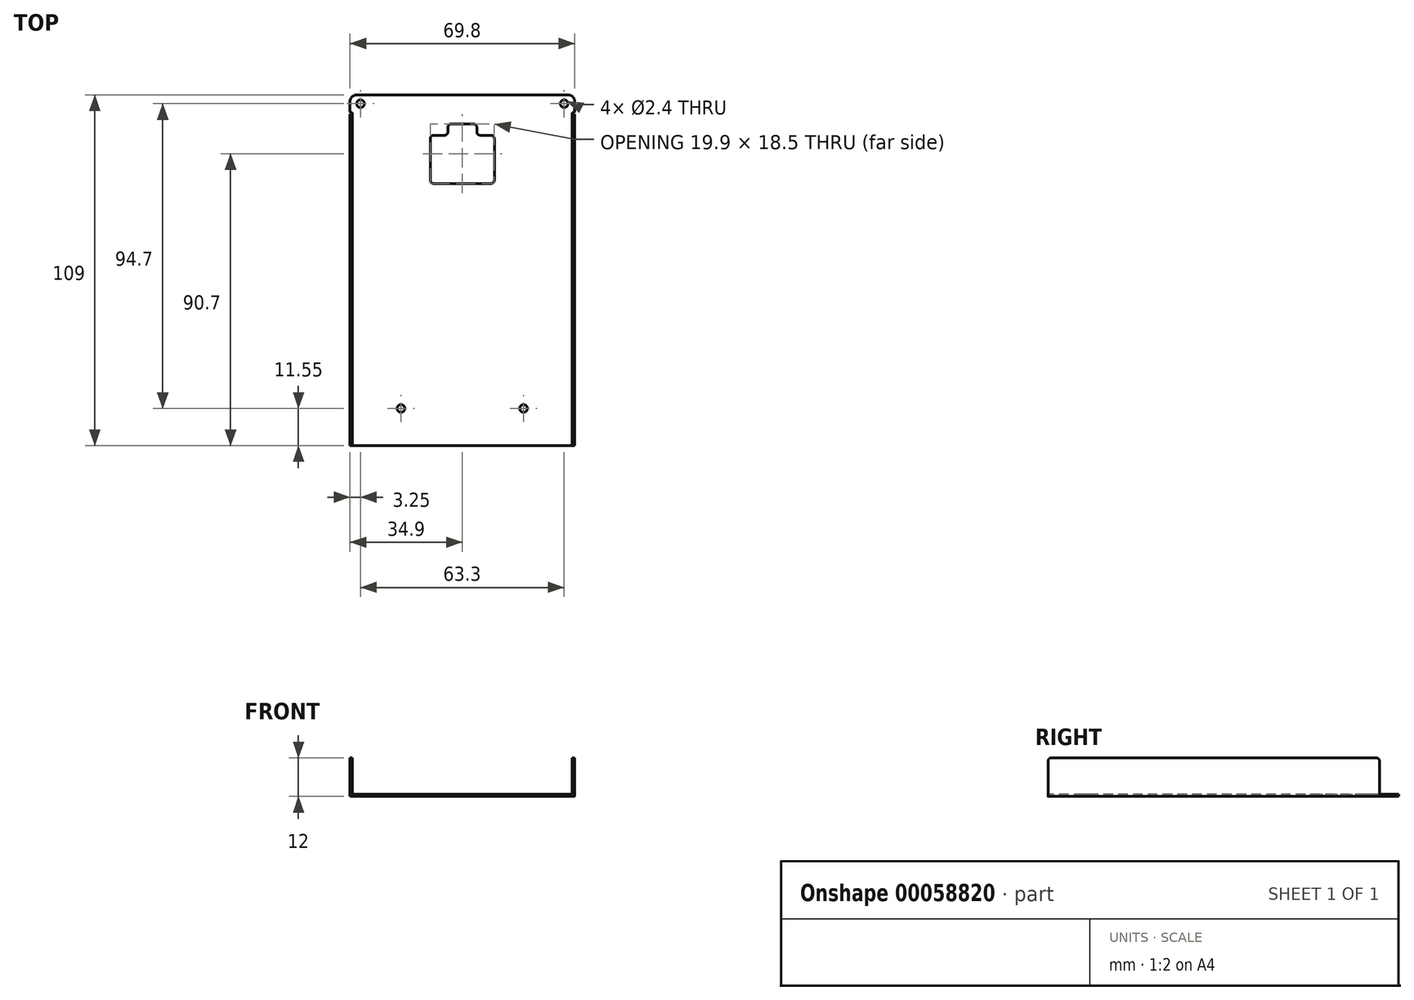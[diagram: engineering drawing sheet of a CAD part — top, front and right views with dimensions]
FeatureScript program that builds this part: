
annotation { "Feature Type Name" : "Feature", "Feature Type Description" : "" }
export const myFeature = defineFeature(function(context is Context, id is Id, definition is map)
    precondition{}
    {
        {
            assignVariable(context, id + "F0", {"name" : "MaterialThickness", "anyValue" : 0.74 * mm});
        }
        {
            var Q0;
            Q0=qCreatedBy(makeId("Top.planeOp"),FACE);
            var sketch = newSketch(context, id + "F1", { "sketchPlane" : qUnion([Q0])});
            skLineSegment(sketch, "E0", {"start": v(30.3, -54.5) * mm, "end": v(30.3, 52.5) * mm});
            skLineSegment(sketch, "E1", {"start": v(-39.5, -54.5) * mm, "end": v(-39.5, 52.5) * mm});
            skLineSegment(sketch, "E2", {"start": v(-37.5, 54.5) * mm, "end": v(28.3, 54.5) * mm});
            skLineSegment(sketch, "E3", {"start": v(-39.5, -54.5) * mm, "end": v(30.3, -54.5) * mm});
            skCircle(sketch, "E4", {"center": v(-36.25, 51.75) * mm, "radius": 1.2 * mm});
            skCircle(sketch, "E5", {"center": v(27.05, 51.75) * mm, "radius": 1.2 * mm});
            skCircle(sketch, "E6", {"center": v(14.45, -42.95) * mm, "radius": 1.2 * mm});
            skCircle(sketch, "E7", {"center": v(-23.65, -42.95) * mm, "radius": 1.2 * mm});
            skPoint(sketch, "E8.visualSharp", {"position": v(-39.5, 54.5) * mm});
            skArc(sketch, "E8.filletArc", {"start": v(-37.5, 54.5) * mm, "mid": v(-38.91, 53.91) * mm, "end": v(-39.5, 52.5) * mm});
            skPoint(sketch, "E9.visualSharp", {"position": v(30.3, 54.5) * mm});
            skArc(sketch, "E9.filletArc", {"start": v(30.3, 52.5) * mm, "mid": v(29.71, 53.91) * mm, "end": v(28.3, 54.5) * mm});
            skLineSegment(sketch, "E10.rect.bottom", {"start": v(3.75, 31.45) * mm, "end": v(-12.95, 31.45) * mm, "construction": true});
            skLineSegment(sketch, "E10.rect.top", {"start": v(3.75, 37.95) * mm, "end": v(-12.95, 37.95) * mm, "construction": true});
            skLineSegment(sketch, "E10.rect.left", {"start": v(3.75, 31.45) * mm, "end": v(3.75, 37.95) * mm, "construction": true});
            skLineSegment(sketch, "E10.rect.right", {"start": v(-12.95, 31.45) * mm, "end": v(-12.95, 37.95) * mm, "construction": true});
            skPoint(sketch, "E10.rect.middle", {"position": v(-4.6, 34.7) * mm});
            skPoint(sketch, "E11.visualSharp", {"position": v(-12.95, 37.95) * mm});
            skPoint(sketch, "E12.visualSharp", {"position": v(-12.95, 31.45) * mm});
            skPoint(sketch, "E13.visualSharp", {"position": v(3.75, 31.45) * mm});
            skPoint(sketch, "E14.visualSharp", {"position": v(3.75, 37.95) * mm});
            skLineSegment(sketch, "E15", {"start": v(-4.6, 54.5) * mm, "end": v(-4.6, 0) * mm, "construction": true});
            skPoint(sketch, "E15.endSnap0", {"position": v(-4.6, 29.15) * mm});
            skLineSegment(sketch, "E16.0", {"start": v(4.35, 41.95) * mm, "end": v(0.9, 41.95) * mm});
            skLineSegment(sketch, "E16.1", {"start": v(5.35, 27.95) * mm, "end": v(5.35, 40.95) * mm});
            skLineSegment(sketch, "E16.2", {"start": v(4.35, 26.95) * mm, "end": v(-13.55, 26.95) * mm});
            skLineSegment(sketch, "E16.3", {"start": v(-14.55, 27.95) * mm, "end": v(-14.55, 40.95) * mm});
            skLineSegment(sketch, "E17", {"start": v(-4.6, 45.45) * mm, "end": v(-8.1, 45.45) * mm});
            skLineSegment(sketch, "E18", {"start": v(-9.1, 44.45) * mm, "end": v(-9.1, 42.95) * mm});
            skLineSegment(sketch, "E19.MirrorCS", {"start": v(-4.6, 45.45) * mm, "end": v(-1.1, 45.45) * mm});
            skLineSegment(sketch, "E20.MirrorCS", {"start": v(-0.1, 44.45) * mm, "end": v(-0.1, 42.95) * mm});
            skLineSegment(sketch, "E21.trimOffspring", {"start": v(-10.1, 41.95) * mm, "end": v(-13.55, 41.95) * mm});
            skPoint(sketch, "E22.visualSharp", {"position": v(-9.1, 45.45) * mm});
            skArc(sketch, "E22.filletArc", {"start": v(-8.1, 45.45) * mm, "mid": v(-8.8, 45.16) * mm, "end": v(-9.1, 44.45) * mm});
            skPoint(sketch, "E23.visualSharp", {"position": v(-0.1, 45.45) * mm});
            skArc(sketch, "E23.filletArc", {"start": v(-0.1, 44.45) * mm, "mid": v(-0.4, 45.16) * mm, "end": v(-1.1, 45.45) * mm});
            skPoint(sketch, "E24.visualSharp", {"position": v(5.35, 41.95) * mm});
            skArc(sketch, "E24.filletArc", {"start": v(5.35, 40.95) * mm, "mid": v(5.06, 41.66) * mm, "end": v(4.35, 41.95) * mm});
            skPoint(sketch, "E25.visualSharp", {"position": v(-14.55, 41.95) * mm});
            skArc(sketch, "E25.filletArc", {"start": v(-13.55, 41.95) * mm, "mid": v(-14.26, 41.66) * mm, "end": v(-14.55, 40.95) * mm});
            skPoint(sketch, "E26.visualSharp", {"position": v(-14.55, 26.95) * mm});
            skArc(sketch, "E26.filletArc", {"start": v(-14.55, 27.95) * mm, "mid": v(-14.26, 27.24) * mm, "end": v(-13.55, 26.95) * mm});
            skPoint(sketch, "E27.visualSharp", {"position": v(5.35, 26.95) * mm});
            skArc(sketch, "E27.filletArc", {"start": v(4.35, 26.95) * mm, "mid": v(5.06, 27.24) * mm, "end": v(5.35, 27.95) * mm});
            skPoint(sketch, "E28.visualSharp", {"position": v(-9.1, 41.95) * mm});
            skArc(sketch, "E28.filletArc", {"start": v(-10.1, 41.95) * mm, "mid": v(-9.4, 42.24) * mm, "end": v(-9.1, 42.95) * mm});
            skPoint(sketch, "E29.visualSharp", {"position": v(-0.1, 41.95) * mm});
            skArc(sketch, "E29.filletArc", {"start": v(-0.1, 42.95) * mm, "mid": v(0.2, 42.24) * mm, "end": v(0.9, 41.95) * mm});
            skSolve(sketch);
        }
        {
            var Q0;
            Q0=qSketchRegion(id+"F1",true);
            extrude(context, id + "F2", {"entities" : qUnion([Q0]), "depth" : getVariable(context, 'MaterialThickness')});
        }
        {
            var Q0;
            Q0=makeQuery(id+"F2.opExtrude","CAP_FACE",FACE,{"disambiguationData":[OSD([sQuery(id+"F1.wireOp",EDGE,"E0"),sQuery(id+"F1.wireOp",EDGE,"E1"),sQuery(id+"F1.wireOp",EDGE,"E2"),sQuery(id+"F1.wireOp",EDGE,"6f542626-f2fe-4e62-9dc8-af51138589b2"),sQuery(id+"F1.wireOp",EDGE,"d65317cd-7c6a-42e4-b09b-290c2fcee52c"),sQuery(id+"F1.wireOp",EDGE,"40293471-6695-460b-ad5e-70b06ef1c56a"),sQuery(id+"F1.wireOp",EDGE,"0b21d12f-ddd4-4e10-89e9-105603cf3b6e"),sQuery(id+"F1.wireOp",EDGE,"79ee2fa8-379d-4bab-a302-94835cc6177e"),sQuery(id+"F1.wireOp",EDGE,"5b2d6fb2-da7a-4bf0-967d-20eb2f197081"),sQuery(id+"F1.wireOp",EDGE,"58eab4bf-ed62-4cde-a4af-ce179843e936"),sQuery(id+"F1.wireOp",EDGE,"bd959c86-ba9c-48ce-8a67-1202fe78da0e"),sQuery(id+"F1.wireOp",EDGE,"4cee920a-c67d-4b1d-aa53-96ac32e3495d"),sQuery(id+"F1.wireOp",EDGE,"0f1fe42c-9a65-4718-9d6c-7e304eec8dc9"),sQuery(id+"F1.wireOp",EDGE,"41df9827-cfb7-4644-8396-7d36da1e9611"),sQuery(id+"F1.wireOp",EDGE,"012ba0f6-2408-4579-9935-ac00b418ca78"),sQuery(id+"F1.wireOp",EDGE,"a6d1a8ff-5993-4480-aa68-b251ac2e3773"),sQuery(id+"F1.wireOp",EDGE,"90826518-7ab9-4a11-9cb2-50551e0b17c5"),sQuery(id+"F1.wireOp",EDGE,"dec4adf2-c5f8-4cf7-9b65-f65938c339f3"),sQuery(id+"F1.wireOp",EDGE,"6aff881b-a8da-4633-8748-1f352a3986aa"),sQuery(id+"F1.wireOp",EDGE,"6b8bf9ce-d740-4018-889f-3fed14afc211"),sQuery(id+"F1.wireOp",EDGE,"4c5e473f-9d43-4600-b7a0-6199b0060a3d"),sQuery(id+"F1.wireOp",EDGE,"50cb06d5-be9d-4216-865b-45e0080ed08e"),sQuery(id+"F1.wireOp",EDGE,"7cdb9ee0-e2e8-45ac-8bdb-5b1d0834dcd6"),sQuery(id+"F1.wireOp",EDGE,"752c73df-f6f7-48e6-814b-9abc70d4c3b5"),sQuery(id+"F1.wireOp",EDGE,"d4403edb-6ecc-4fb8-9abe-a5cf43e54ecf"),sQuery(id+"F1.wireOp",EDGE,"191c357e-7506-4e18-90b4-bb71a73d584a"),sQuery(id+"F1.wireOp",EDGE,"36182ddf-d56b-4a3d-8339-a1267bb4d182"),sQuery(id+"F1.wireOp",EDGE,"3cfc1f5f-f39c-4474-8388-3dd97f5584c0"),sQuery(id+"F1.wireOp",EDGE,"4c48c394-4fa5-4c5e-9177-710229550736"),sQuery(id+"F1.wireOp",EDGE,"7cbb6381-f1a6-487e-88ab-7a4eef711d66"),sQuery(id+"F1.wireOp",EDGE,"5dec03ee-e572-469c-8b05-a0337d8c623c"),sQuery(id+"F1.wireOp",EDGE,"d16cefb8-363f-4407-b9f5-a53e7ae9c1b3"),sQuery(id+"F1.wireOp",EDGE,"E3"),sQuery(id+"F1.wireOp",EDGE,"E4"),sQuery(id+"F1.wireOp",EDGE,"E5"),sQuery(id+"F1.wireOp",EDGE,"E6"),sQuery(id+"F1.wireOp",EDGE,"E7"),sQuery(id+"F1.wireOp",EDGE,"49b4b471-93f8-46f3-9035-a445390ed24f"),sQuery(id+"F1.wireOp",EDGE,"013d988c-518a-43cd-931a-afb82e042039"),sQuery(id+"F1.wireOp",EDGE,"b009fba4-9d74-487f-b1b2-e77be794c7df"),sQuery(id+"F1.wireOp",EDGE,"f28ca319-59c4-4176-9a6a-b8e9c12ca7b2"),sQuery(id+"F1.wireOp",EDGE,"59ab4c71-fb57-451b-a7bc-e024e530d7a6"),sQuery(id+"F1.wireOp",EDGE,"47252107-bac6-4eb8-93b8-c023fa44c8e8"),sQuery(id+"F1.wireOp",EDGE,"b80df239-3f1f-4e86-9030-635545e30786"),sQuery(id+"F1.wireOp",EDGE,"baca6f1a-d7fb-4206-b7a5-cbdfadded3ed"),sQuery(id+"F1.wireOp",EDGE,"d976eecf-eaf4-4cce-8532-cadcb9868e27"),sQuery(id+"F1.wireOp",EDGE,"4569245a-5ea1-4106-908f-afcd5ec1f1bc"),sQuery(id+"F1.wireOp",EDGE,"a88b5052-fa65-4c67-8c1e-17682c5e5b6b"),sQuery(id+"F1.wireOp",EDGE,"c3202e9f-e72c-49b5-b375-3782fcdd84b2"),sQuery(id+"F1.wireOp",EDGE,"ae9a4485-fe66-418c-99cf-f2badf27484e"),sQuery(id+"F1.wireOp",EDGE,"40ff1a60-ad1b-470d-9941-3648aebe8ce7"),sQuery(id+"F1.wireOp",EDGE,"7efc5e7b-d0f8-4c2e-be74-3157bb2b81f2"),sQuery(id+"F1.wireOp",EDGE,"a604e65e-d63e-4fcf-87a2-1d68459ffd2f"),sQuery(id+"F1.wireOp",EDGE,"9b040391-65f2-4517-89ec-09136afad379"),sQuery(id+"F1.wireOp",EDGE,"e81865d5-4931-4b27-a9b8-568d70e091ed"),sQuery(id+"F1.wireOp",EDGE,"33fbec23-d60a-44ca-a5ed-6a9adadaf32d"),sQuery(id+"F1.wireOp",EDGE,"d18368f3-3517-4bad-a039-cce0df7d30f8"),sQuery(id+"F1.wireOp",EDGE,"adf0adf2-995a-4c73-9a9f-0c34d5a06e90"),sQuery(id+"F1.wireOp",EDGE,"8d4f8d75-ff03-45a9-8da5-e2bfa5d89cf8"),sQuery(id+"F1.wireOp",EDGE,"0def6ea3-42c0-499a-87a9-d967d37a2398"),sQuery(id+"F1.wireOp",EDGE,"418a7f11-9ba6-4330-9219-449a15997eb1"),sQuery(id+"F1.wireOp",EDGE,"19beec09-856a-4503-8090-15e2c865af76"),sQuery(id+"F1.wireOp",EDGE,"f8c1126e-abe4-42b3-b083-fbb39cc2f8dd"),sQuery(id+"F1.wireOp",EDGE,"511b526c-3d0c-4ee1-8060-97b439644142"),sQuery(id+"F1.wireOp",EDGE,"77a7ece0-8d82-497c-bc19-0a22f7db5636"),sQuery(id+"F1.wireOp",EDGE,"9b200ce0-63a7-49f5-a05a-f950ba5009f6"),sQuery(id+"F1.wireOp",EDGE,"11c32315-20c8-4d77-a798-f002eaef5331"),sQuery(id+"F1.wireOp",EDGE,"23f4386d-157d-49f5-b0b6-e080ac96bcf1"),sQuery(id+"F1.wireOp",EDGE,"c1e70f36-b0bc-4dd7-b00e-9526c5c15aa3"),sQuery(id+"F1.wireOp",EDGE,"f1081c25-ebe6-49c4-9bd5-8d7a2e5cd1f3"),sQuery(id+"F1.wireOp",EDGE,"baca9122-060d-4abe-9427-23689144884f"),sQuery(id+"F1.wireOp",EDGE,"E8.filletArc"),sQuery(id+"F1.wireOp",EDGE,"E9.filletArc")])],"isStart":true});
            var sketch = newSketch(context, id + "F3", { "sketchPlane" : qUnion([Q0])});
            skLineSegment(sketch, "E30.bottom", {"start": v(30.3, 54.5) * mm, "end": v(29.56, 54.5) * mm});
            skLineSegment(sketch, "E30.top", {"start": v(30.3, -48.5) * mm, "end": v(29.56, -48.5) * mm});
            skLineSegment(sketch, "E30.left", {"start": v(30.3, 54.5) * mm, "end": v(30.3, -48.5) * mm});
            skLineSegment(sketch, "E30.right", {"start": v(29.56, 54.5) * mm, "end": v(29.56, -48.5) * mm});
            skLineSegment(sketch, "E31.bottom", {"start": v(-39.5, 54.5) * mm, "end": v(-38.76, 54.5) * mm});
            skLineSegment(sketch, "E31.top", {"start": v(-39.5, -48.5) * mm, "end": v(-38.76, -48.5) * mm});
            skLineSegment(sketch, "E31.left", {"start": v(-39.5, 54.5) * mm, "end": v(-39.5, -48.5) * mm});
            skLineSegment(sketch, "E31.right", {"start": v(-38.76, 54.5) * mm, "end": v(-38.76, -48.5) * mm});
            skSolve(sketch);
        }
        {
            var Q0;
            Q0=qSketchRegion(id+"F3",true);
            extrude(context, id + "F4", {"entities" : qUnion([Q0]), "operationType" : NewBodyOperationType.ADD, "oppositeDirection" : true, "depth" : 12 * mm});
        }
        {
            var Q0;
            Q0=makeQuery(id+"F4.opExtrude","CAP_EDGE",EDGE,{"disambiguationData":[OSD([sQuery(id+"F3.wireOp",EDGE,"E30.bottom")])],"isStart":false});
            var Q1;
            Q1=makeQuery(id+"F4.opExtrude","CAP_EDGE",EDGE,{"disambiguationData":[OSD([sQuery(id+"F3.wireOp",EDGE,"E30.top")])],"isStart":false});
            var Q2;
            Q2=makeQuery(id+"F4.opExtrude","CAP_EDGE",EDGE,{"disambiguationData":[OSD([sQuery(id+"F3.wireOp",EDGE,"E31.top")])],"isStart":false});
            var Q3;
            Q3=makeQuery(id+"F4.opExtrude","CAP_EDGE",EDGE,{"disambiguationData":[OSD([sQuery(id+"F3.wireOp",EDGE,"E31.bottom")])],"isStart":false});
            fillet(context, id + "F5", {"entities" : qUnion([Q0, Q1, Q2, Q3]), "radius" : 1 * mm, "tangentPropagation" : true, "allowEdgeOverflow" : false});
        }
        {
            var Q0;
            Q0=makeQuery(id+"F2.opExtrude","CAP_FACE",FACE,{"disambiguationData":[OSD([sQuery(id+"F1.wireOp",EDGE,"E0"),sQuery(id+"F1.wireOp",EDGE,"E1"),sQuery(id+"F1.wireOp",EDGE,"E2"),sQuery(id+"F1.wireOp",EDGE,"E3"),sQuery(id+"F1.wireOp",EDGE,"E4"),sQuery(id+"F1.wireOp",EDGE,"E5"),sQuery(id+"F1.wireOp",EDGE,"E6"),sQuery(id+"F1.wireOp",EDGE,"E7"),sQuery(id+"F1.wireOp",EDGE,"E8.filletArc"),sQuery(id+"F1.wireOp",EDGE,"E9.filletArc"),sQuery(id+"F1.wireOp",EDGE,"15ddee82-5b16-4217-afd7-89f68c77764c.0"),sQuery(id+"F1.wireOp",EDGE,"15ddee82-5b16-4217-afd7-89f68c77764c.1"),sQuery(id+"F1.wireOp",EDGE,"15ddee82-5b16-4217-afd7-89f68c77764c.2"),sQuery(id+"F1.wireOp",EDGE,"15ddee82-5b16-4217-afd7-89f68c77764c.3"),sQuery(id+"F1.wireOp",EDGE,"15ddee82-5b16-4217-afd7-89f68c77764c.4"),sQuery(id+"F1.wireOp",EDGE,"15ddee82-5b16-4217-afd7-89f68c77764c.5"),sQuery(id+"F1.wireOp",EDGE,"15ddee82-5b16-4217-afd7-89f68c77764c.6"),sQuery(id+"F1.wireOp",EDGE,"15ddee82-5b16-4217-afd7-89f68c77764c.7")])],"isStart":false});
            var sketch = newSketch(context, id + "F6", { "sketchPlane" : qUnion([Q0])});
            skLineSegment(sketch, "E32.bottom", {"start": v(-39.5, 48.5) * mm, "end": v(-38.76, 48.5) * mm});
            skLineSegment(sketch, "E32.top", {"start": v(-39.5, 49) * mm, "end": v(-38.76, 49) * mm});
            skLineSegment(sketch, "E32.left", {"start": v(-39.5, 48.5) * mm, "end": v(-39.5, 49) * mm});
            skLineSegment(sketch, "E32.right", {"start": v(-38.76, 48.5) * mm, "end": v(-38.76, 49) * mm});
            skLineSegment(sketch, "E33.bottom", {"start": v(30.3, 48.5) * mm, "end": v(29.56, 48.5) * mm});
            skLineSegment(sketch, "E33.top", {"start": v(30.3, 49) * mm, "end": v(29.56, 49) * mm});
            skLineSegment(sketch, "E33.left", {"start": v(30.3, 48.5) * mm, "end": v(30.3, 49) * mm});
            skLineSegment(sketch, "E33.right", {"start": v(29.56, 48.5) * mm, "end": v(29.56, 49) * mm});
            skSolve(sketch);
        }
        {
            var Q0;
            Q0=qSketchRegion(id+"F6",true);
            extrude(context, id + "F7", {"entities" : qUnion([Q0]), "operationType" : NewBodyOperationType.REMOVE, "oppositeDirection" : true, "depth" : 25 * mm});
        }
        {
            var Q0;
            Q0=makeQuery(id+"F7.boolean.opBoolean","COPY",EDGE,{"derivedFrom":makeQuery(id+"F7.opExtrude","SWEPT_EDGE",EDGE,{"disambiguationData":[OSD([sQuery(id+"F1.wireOp",EDGE,"E0"),sQuery(id+"F6.wireOp",EDGE,"E33.top"),sQuery(id+"F6.wireOp",EDGE,"E33.left")])]})});
            var Q1;
            Q1=makeQuery(id+"F7.boolean.opBoolean","COPY",EDGE,{"derivedFrom":makeQuery(id+"F7.opExtrude","SWEPT_EDGE",EDGE,{"disambiguationData":[OSD([sQuery(id+"F6.wireOp",EDGE,"E33.top"),sQuery(id+"F6.wireOp",EDGE,"E33.right")])]})});
            var Q2;
            Q2=makeQuery(id+"F7.boolean.opBoolean","COPY",EDGE,{"derivedFrom":makeQuery(id+"F7.opExtrude","SWEPT_EDGE",EDGE,{"disambiguationData":[OSD([sQuery(id+"F1.wireOp",EDGE,"E1"),sQuery(id+"F6.wireOp",EDGE,"E32.top"),sQuery(id+"F6.wireOp",EDGE,"E32.left")])]})});
            var Q3;
            Q3=makeQuery(id+"F7.boolean.opBoolean","COPY",EDGE,{"derivedFrom":makeQuery(id+"F7.opExtrude","SWEPT_EDGE",EDGE,{"disambiguationData":[OSD([sQuery(id+"F6.wireOp",EDGE,"E32.top"),sQuery(id+"F6.wireOp",EDGE,"E32.right")])]})});
            fillet(context, id + "F8", {"entities" : qUnion([Q0, Q1, Q2, Q3]), "radius" : .3 * mm, "tangentPropagation" : true, "allowEdgeOverflow" : false});
        }
        {
            var Q0;
            {var subQ0=sQuery(id+"F1.wireOp",EDGE,"E3");var subQ1=sQuery(id+"F1.wireOp",EDGE,"E1");Q0=makeQuery(id+"F7.boolean.opBoolean","SPLIT",EDGE,{"disambiguationData":[TD([makeQuery(id+"F2.opExtrude","SWEPT_FACE",FACE,{"disambiguationData":[OSD([subQ0])]})])],"derivedFrom":makeQuery(id+"F2.opExtrude","CAP_EDGE",EDGE,{"disambiguationData":[OSD([subQ1])],"isStart":true})});}
            var Q1;
            {var subQ0=sQuery(id+"F1.wireOp",EDGE,"E3");var subQ1=sQuery(id+"F1.wireOp",EDGE,"E0");Q1=makeQuery(id+"F7.boolean.opBoolean","SPLIT",EDGE,{"disambiguationData":[TD([makeQuery(id+"F2.opExtrude","SWEPT_FACE",FACE,{"disambiguationData":[OSD([subQ0])]})])],"derivedFrom":makeQuery(id+"F2.opExtrude","CAP_EDGE",EDGE,{"disambiguationData":[OSD([subQ1])],"isStart":true})});}
            fillet(context, id + "F9", {"entities" : qUnion([Q0, Q1]), "radius" : .65 * mm, "tangentPropagation" : true, "allowEdgeOverflow" : false});
        }
        {
            var Q0;
            Q0=makeQuery(id+"F4.boolean.opBoolean","INTERSECT",EDGE,{"derivedFrom":[makeQuery(id+"F2.opExtrude","CAP_FACE",FACE,{"disambiguationData":[OSD([sQuery(id+"F1.wireOp",EDGE,"E0"),sQuery(id+"F1.wireOp",EDGE,"E1"),sQuery(id+"F1.wireOp",EDGE,"E2"),sQuery(id+"F1.wireOp",EDGE,"E3"),sQuery(id+"F1.wireOp",EDGE,"E4"),sQuery(id+"F1.wireOp",EDGE,"E5"),sQuery(id+"F1.wireOp",EDGE,"E6"),sQuery(id+"F1.wireOp",EDGE,"E7"),sQuery(id+"F1.wireOp",EDGE,"E8.filletArc"),sQuery(id+"F1.wireOp",EDGE,"E9.filletArc"),sQuery(id+"F1.wireOp",EDGE,"15ddee82-5b16-4217-afd7-89f68c77764c.0"),sQuery(id+"F1.wireOp",EDGE,"15ddee82-5b16-4217-afd7-89f68c77764c.1"),sQuery(id+"F1.wireOp",EDGE,"15ddee82-5b16-4217-afd7-89f68c77764c.2"),sQuery(id+"F1.wireOp",EDGE,"15ddee82-5b16-4217-afd7-89f68c77764c.3"),sQuery(id+"F1.wireOp",EDGE,"15ddee82-5b16-4217-afd7-89f68c77764c.4"),sQuery(id+"F1.wireOp",EDGE,"15ddee82-5b16-4217-afd7-89f68c77764c.5"),sQuery(id+"F1.wireOp",EDGE,"15ddee82-5b16-4217-afd7-89f68c77764c.6"),sQuery(id+"F1.wireOp",EDGE,"15ddee82-5b16-4217-afd7-89f68c77764c.7")])],"isStart":false}),makeQuery(id+"F4.opExtrude","SWEPT_FACE",FACE,{"disambiguationData":[OSD([sQuery(id+"F3.wireOp",EDGE,"E31.right")])]})]});
            var Q1;
            Q1=makeQuery(id+"F4.boolean.opBoolean","INTERSECT",EDGE,{"derivedFrom":[makeQuery(id+"F2.opExtrude","CAP_FACE",FACE,{"disambiguationData":[OSD([sQuery(id+"F1.wireOp",EDGE,"E0"),sQuery(id+"F1.wireOp",EDGE,"E1"),sQuery(id+"F1.wireOp",EDGE,"E2"),sQuery(id+"F1.wireOp",EDGE,"E3"),sQuery(id+"F1.wireOp",EDGE,"E4"),sQuery(id+"F1.wireOp",EDGE,"E5"),sQuery(id+"F1.wireOp",EDGE,"E6"),sQuery(id+"F1.wireOp",EDGE,"E7"),sQuery(id+"F1.wireOp",EDGE,"E8.filletArc"),sQuery(id+"F1.wireOp",EDGE,"E9.filletArc"),sQuery(id+"F1.wireOp",EDGE,"15ddee82-5b16-4217-afd7-89f68c77764c.0"),sQuery(id+"F1.wireOp",EDGE,"15ddee82-5b16-4217-afd7-89f68c77764c.1"),sQuery(id+"F1.wireOp",EDGE,"15ddee82-5b16-4217-afd7-89f68c77764c.2"),sQuery(id+"F1.wireOp",EDGE,"15ddee82-5b16-4217-afd7-89f68c77764c.3"),sQuery(id+"F1.wireOp",EDGE,"15ddee82-5b16-4217-afd7-89f68c77764c.4"),sQuery(id+"F1.wireOp",EDGE,"15ddee82-5b16-4217-afd7-89f68c77764c.5"),sQuery(id+"F1.wireOp",EDGE,"15ddee82-5b16-4217-afd7-89f68c77764c.6"),sQuery(id+"F1.wireOp",EDGE,"15ddee82-5b16-4217-afd7-89f68c77764c.7")])],"isStart":false}),makeQuery(id+"F4.opExtrude","SWEPT_FACE",FACE,{"disambiguationData":[OSD([sQuery(id+"F3.wireOp",EDGE,"E30.right")])]})]});
            fillet(context, id + "F10", {"entities" : qUnion([Q0, Q1]), "radius" : .3 * mm, "tangentPropagation" : true, "allowEdgeOverflow" : false});
        }
    });
